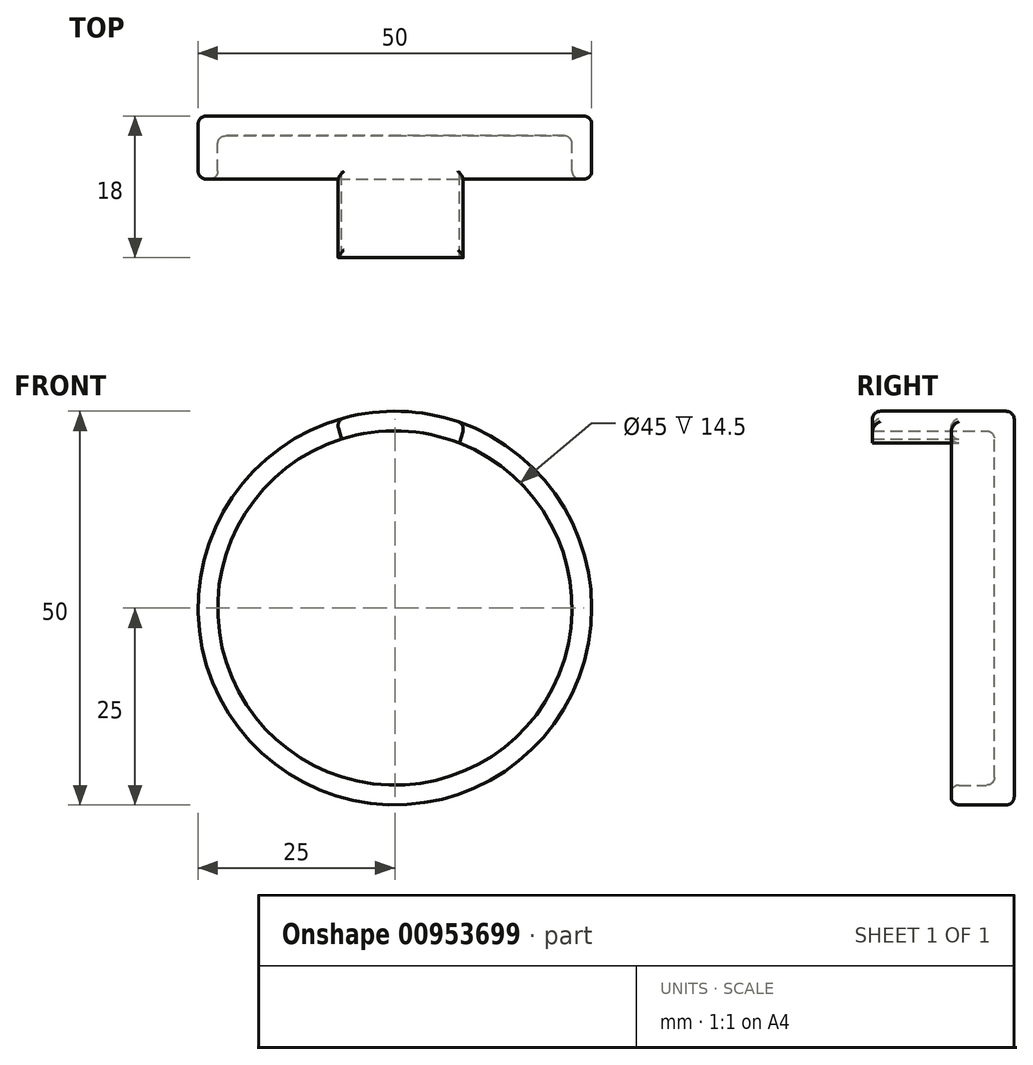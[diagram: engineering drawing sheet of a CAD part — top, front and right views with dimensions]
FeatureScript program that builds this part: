
annotation { "Feature Type Name" : "Feature", "Feature Type Description" : "" }
export const myFeature = defineFeature(function(context is Context, id is Id, definition is map)
    precondition{}
    {
        {
            var Q0;
            Q0=qCreatedBy(makeId("Front.planeOp"),FACE);
            var sketch = newSketch(context, id + "F0", { "sketchPlane" : qUnion([Q0])});
            skCircle(sketch, "E0", {"center": v(0, 0) * mm, "radius": 25 * mm});
            skSolve(sketch);
        }
        {
            var Q0;
            Q0 = qSketchRegion(id + "F0", true);
            extrude(context, id + "F1", {"entities" : qUnion([Q0]), "depth" : 8 * mm, "offsetDistance" : 25 * mm});
        }
        {
            var Q0;
            Q0=makeQuery(id+"F1.opExtrude","CAP_FACE",FACE,{"disambiguationData":[OSD([sQuery(id+"F0.wireOp",EDGE,"E0")])],"isStart":false});
            shell(context, id + "F2", {"entities" : qUnion([Q0]), "thickness" : 2.5 * mm});
        }
        {
            var Q0;
            Q0=makeQuery(id+"F1.opExtrude","CAP_FACE",FACE,{"disambiguationData":[OSD([sQuery(id+"F0.wireOp",EDGE,"E0")])],"isStart":false});
            var sketch = newSketch(context, id + "F3", { "sketchPlane" : qUnion([Q0])});
            skLineSegment(sketch, "E1", {"start": v(-6.77, 21.46) * mm, "end": v(-7.46, 23.86) * mm});
            skLineSegment(sketch, "E2", {"start": v(8.23, 20.94) * mm, "end": v(8.89, 23.37) * mm});
            skArc(sketch, "E3", {"start": v(8.23, 20.94) * mm, "mid": v(0.77, 22.49) * mm, "end": v(-6.77, 21.46) * mm});
            skArc(sketch, "E4", {"start": v(8.89, 23.37) * mm, "mid": v(0.75, 24.99) * mm, "end": v(-7.46, 23.86) * mm});
            skSolve(sketch);
        }
        {
            var Q0;
            Q0=makeQuery(id+"F3.imprint","IMPRINT",FACE,{"disambiguationData":[TD([[makeQuery(id+"F3.imprint","IMPRINT",EDGE,{"derivedFrom":sQuery(id+"F3.wireOp",EDGE,"E1")}),-1.0]])]});
            extrude(context, id + "F4", {"entities" : qUnion([Q0]), "operationType" : NewBodyOperationType.ADD, "depth" : 10 * mm, "offsetDistance" : 25 * mm});
        }
        {
            var Q0;
            {var subQ0=sQuery(id+"F0.wireOp",EDGE,"E0");Q0=makeQuery(id+"F2.opShell","OFFSET_FACE",FACE,{"disambiguationData":[OSD([subQ0]),TDD([makeQuery(id+"F1.opExtrude","CAP_FACE",FACE,{"disambiguationData":[OSD([subQ0])],"isStart":true})])]});}
            var Q1;
            {var subQ0=sQuery(id+"F0.wireOp",EDGE,"E0");Q1=makeQuery(id+"F2.opShell","OFFSET_EDGE",EDGE,{"disambiguationData":[OSD([subQ0]),TDD([makeQuery(id+"F1.opExtrude","CAP_EDGE",EDGE,{"disambiguationData":[OSD([subQ0])],"isStart":false})])]});}
            var Q2;
            Q2=makeQuery(id+"F1.opExtrude","CAP_EDGE",EDGE,{"disambiguationData":[OSD([sQuery(id+"F0.wireOp",EDGE,"E0")])],"isStart":true});
            var Q3;
            Q3=makeQuery(id+"F1.opExtrude","CAP_EDGE",EDGE,{"disambiguationData":[OSD([sQuery(id+"F0.wireOp",EDGE,"E0")])],"isStart":false});
            var Q4;
            Q4=makeQuery(id+"F4.boolean.opBoolean","MERGE",FACE,{"derivedFrom":[makeQuery(id+"F1.opExtrude","SWEPT_FACE",FACE,{"disambiguationData":[OSD([sQuery(id+"F0.wireOp",EDGE,"E0")])]}),makeQuery(id+"F4.opExtrude","SWEPT_FACE",FACE,{"disambiguationData":[OSD([sQuery(id+"F3.wireOp",EDGE,"E4")])]})]});
            fillet(context, id + "F5", {"entities" : qUnion([Q0, Q1, Q2, Q3, Q4]), "radius" : 1 * mm, "tangentPropagation" : true, "allowEdgeOverflow" : false});
        }
    });
